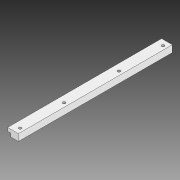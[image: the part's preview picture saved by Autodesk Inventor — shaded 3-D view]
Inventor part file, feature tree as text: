
AUTODESK INVENTOR PART (.ipt)
format: ipt  version: 2020 (Build 240168000, 168)  size: 144,384 bytes
history: native  units: mm
features: extrude x2, sketch x2, fillet x1
ambient origin geometry x8: Origin, YZ Plane, XZ Plane, XY Plane, X Axis, Y Axis, Z Axis, Center Point
bodies: Solid1 (feature_tree)
feature tree (5):
  extrude  "Extrusion1"  Depth=6.0mm
  extrude  "Extrusion2"  Depth=5.5mm
  fillet  "Fillet1"  Radius=280.0mm
  sketch  "Sketch1"  dims[d1=6.3mm d2=6.0mm]
  sketch  "Sketch2"  dims[d4=14.0mm d5=5.5mm d6=280.0mm d7=0.0mm d8=5.0mm d9=10.0mm d10=7.0mm d11=10.0mm d12=7.0mm d13=7.0mm d14=90.0mm d15=5.0mm d16=90.0mm d17=7.0mm d18=0.0mm d19=0.0mm d20=1.0mm]
